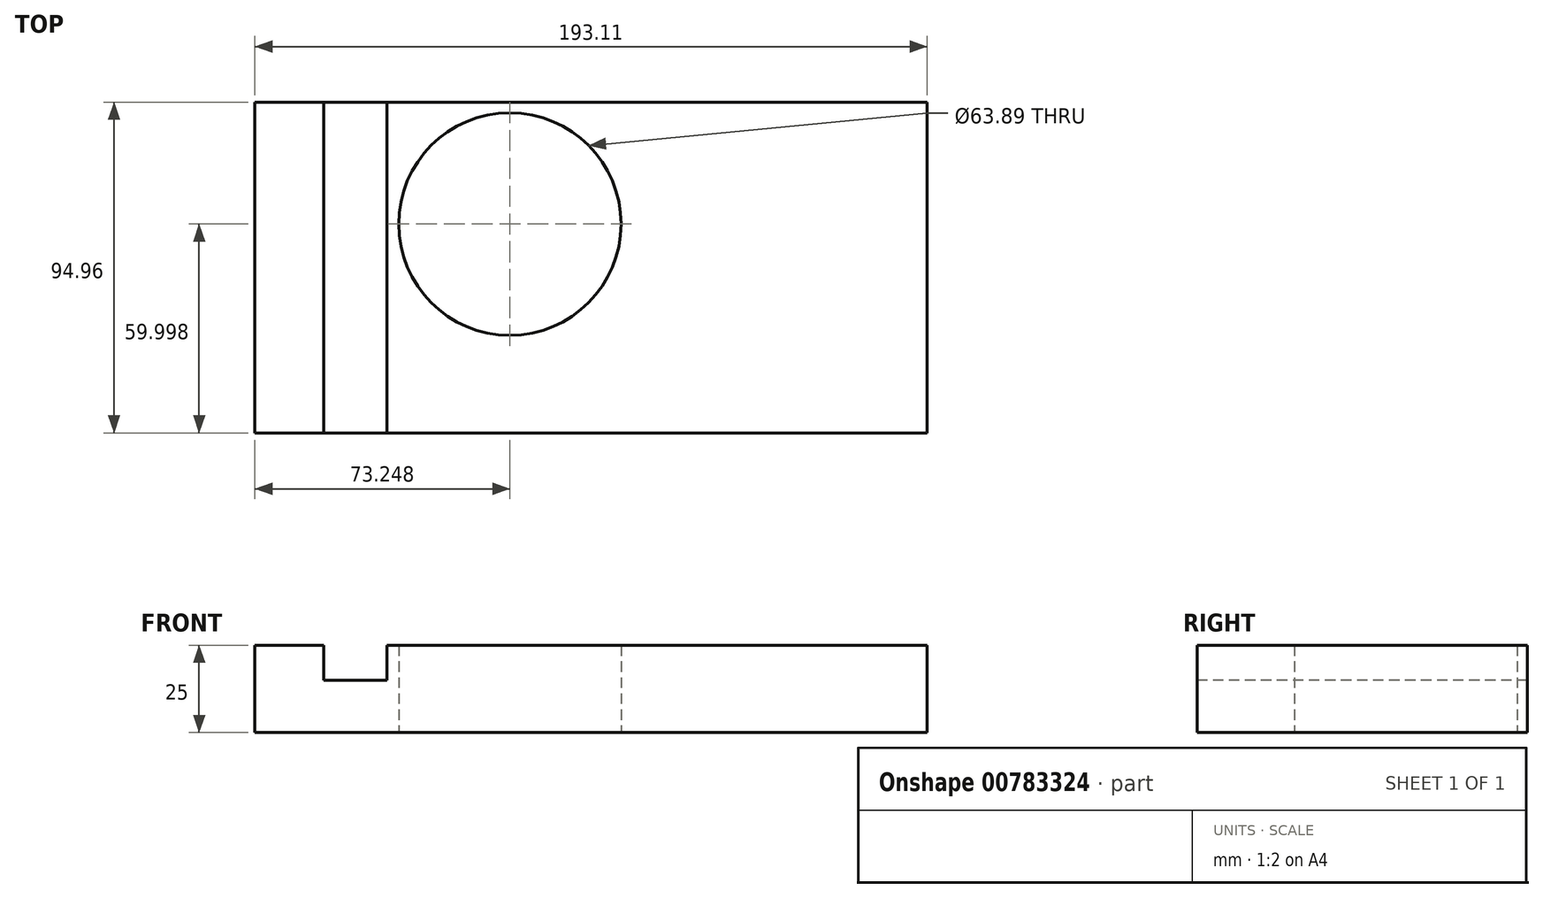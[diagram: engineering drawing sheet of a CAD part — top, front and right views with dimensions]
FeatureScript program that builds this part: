
annotation { "Feature Type Name" : "Feature", "Feature Type Description" : "" }
export const myFeature = defineFeature(function(context is Context, id is Id, definition is map)
    precondition{}
    {
        {
            var Q0;
            Q0=qCreatedBy(makeId("Top.planeOp"),FACE);
            var sketch = newSketch(context, id + "F0", { "sketchPlane" : qUnion([Q0])});
            skLineSegment(sketch, "E0.bottom", {"start": v(-90.13, 44.33) * mm, "end": v(102.98, 44.33) * mm});
            skLineSegment(sketch, "E0.top", {"start": v(-90.13, -50.63) * mm, "end": v(102.98, -50.63) * mm});
            skLineSegment(sketch, "E0.left", {"start": v(-90.13, 44.33) * mm, "end": v(-90.13, -50.63) * mm});
            skLineSegment(sketch, "E0.right", {"start": v(102.98, 44.33) * mm, "end": v(102.98, -50.63) * mm});
            skCircle(sketch, "E1", {"center": v(-16.88, 9.37) * mm, "radius": 31.95 * mm});
            skSolve(sketch);
        }
        {
            var Q0;
            Q0=makeQuery(id+"F0.imprint","IMPRINT",FACE,{"disambiguationData":[TD([[makeQuery(id+"F0.imprint","IMPRINT",EDGE,{"derivedFrom":sQuery(id+"F0.wireOp",EDGE,"E0.bottom")}),-1.0]])]});
            var sketch = newSketch(context, id + "F1", { "sketchPlane" : qUnion([Q0])});
            skSolve(sketch);
        }
        {
            var Q0;
            Q0=makeQuery(id+"F1.imprint","IMPRINT",FACE,{"disambiguationData":[TD([[makeQuery(id+"F1.imprint","IMPRINT",EDGE,{"derivedFrom":makeQuery(id+"F0.imprint","IMPRINT",EDGE,{"derivedFrom":sQuery(id+"F0.wireOp",EDGE,"E0.bottom")})}),-1.0]])]});
            extrude(context, id + "F2", {"entities" : qUnion([Q0]), "depth" : 25 * mm, "offsetDistance" : 25 * mm});
        }
        {
            var Q0;
            Q0=makeQuery(id+"F2.opExtrude","CAP_FACE",FACE,{"disambiguationData":[OSD([sQuery(id+"F0.wireOp",EDGE,"E0.bottom"),sQuery(id+"F0.wireOp",EDGE,"E0.top"),sQuery(id+"F0.wireOp",EDGE,"E0.left"),sQuery(id+"F0.wireOp",EDGE,"E0.right"),sQuery(id+"F0.wireOp",EDGE,"E1")])],"isStart":false});
            var sketch = newSketch(context, id + "F3", { "sketchPlane" : qUnion([Q0])});
            skLineSegment(sketch, "E2.bottom", {"start": v(-70.31, 44.33) * mm, "end": v(-52.25, 44.33) * mm});
            skLineSegment(sketch, "E2.top", {"start": v(-70.31, -50.63) * mm, "end": v(-52.25, -50.63) * mm});
            skLineSegment(sketch, "E2.left", {"start": v(-70.31, 44.33) * mm, "end": v(-70.31, -50.63) * mm});
            skLineSegment(sketch, "E2.right", {"start": v(-52.25, 44.33) * mm, "end": v(-52.25, -50.63) * mm});
            skSolve(sketch);
        }
        {
            var Q0;
            Q0=makeQuery(id+"F3.imprint","IMPRINT",FACE,{"disambiguationData":[TD([[makeQuery(id+"F3.imprint","IMPRINT",EDGE,{"derivedFrom":sQuery(id+"F3.wireOp",EDGE,"E2.bottom")}),-1.0]])]});
            extrude(context, id + "F4", {"entities" : qUnion([Q0]), "operationType" : NewBodyOperationType.REMOVE, "oppositeDirection" : true, "depth" : 10 * mm, "offsetDistance" : 25 * mm});
        }
    });
